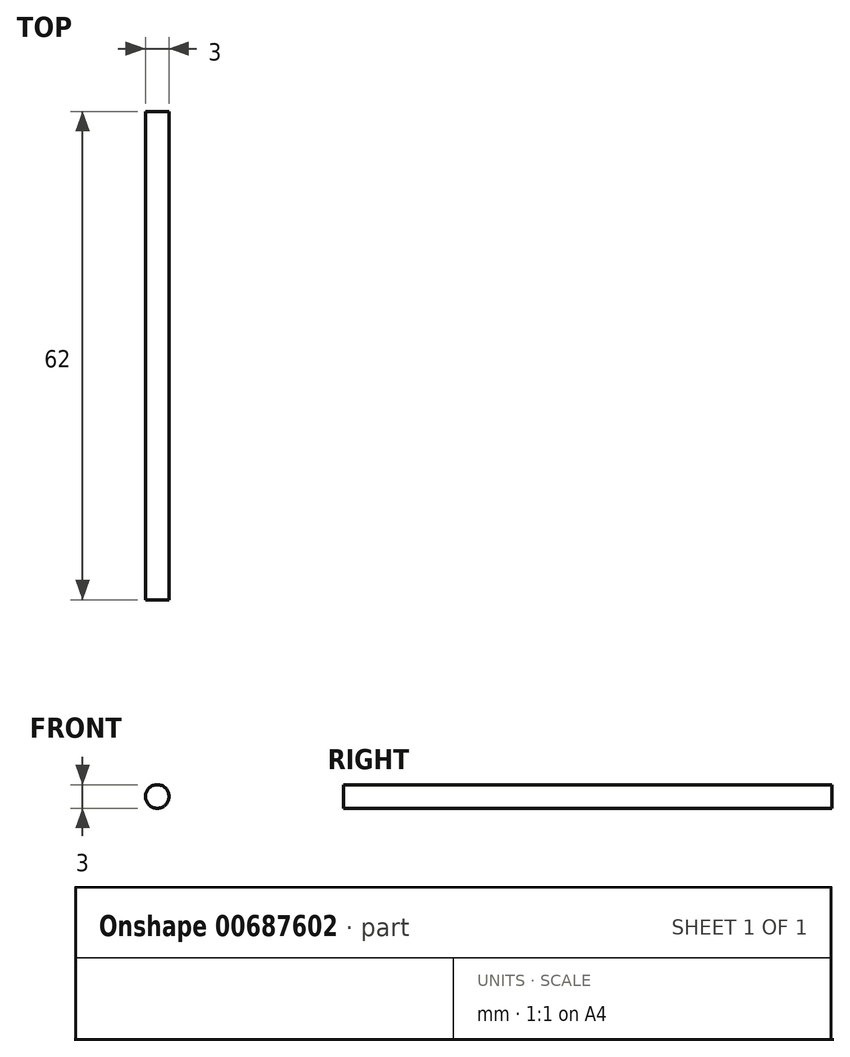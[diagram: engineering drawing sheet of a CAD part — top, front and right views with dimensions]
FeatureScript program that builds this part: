
annotation { "Feature Type Name" : "Feature", "Feature Type Description" : "" }
export const myFeature = defineFeature(function(context is Context, id is Id, definition is map)
    precondition{}
    {
        {
            var Q0;
            Q0=qCreatedBy(makeId("Front.planeOp"),FACE);
            var sketch = newSketch(context, id + "F0", { "sketchPlane" : qUnion([Q0])});
            skCircle(sketch, "E0", {"center": v(0, 0) * mm, "radius": 1.5 * mm});
            skSolve(sketch);
        }
        {
            var Q0;
            Q0 = qSketchRegion(id + "F0", true);
            extrude(context, id + "F1", {"entities" : qUnion([Q0]), "depth" : 62 * mm, "offsetDistance" : 25 * mm});
        }
    });
